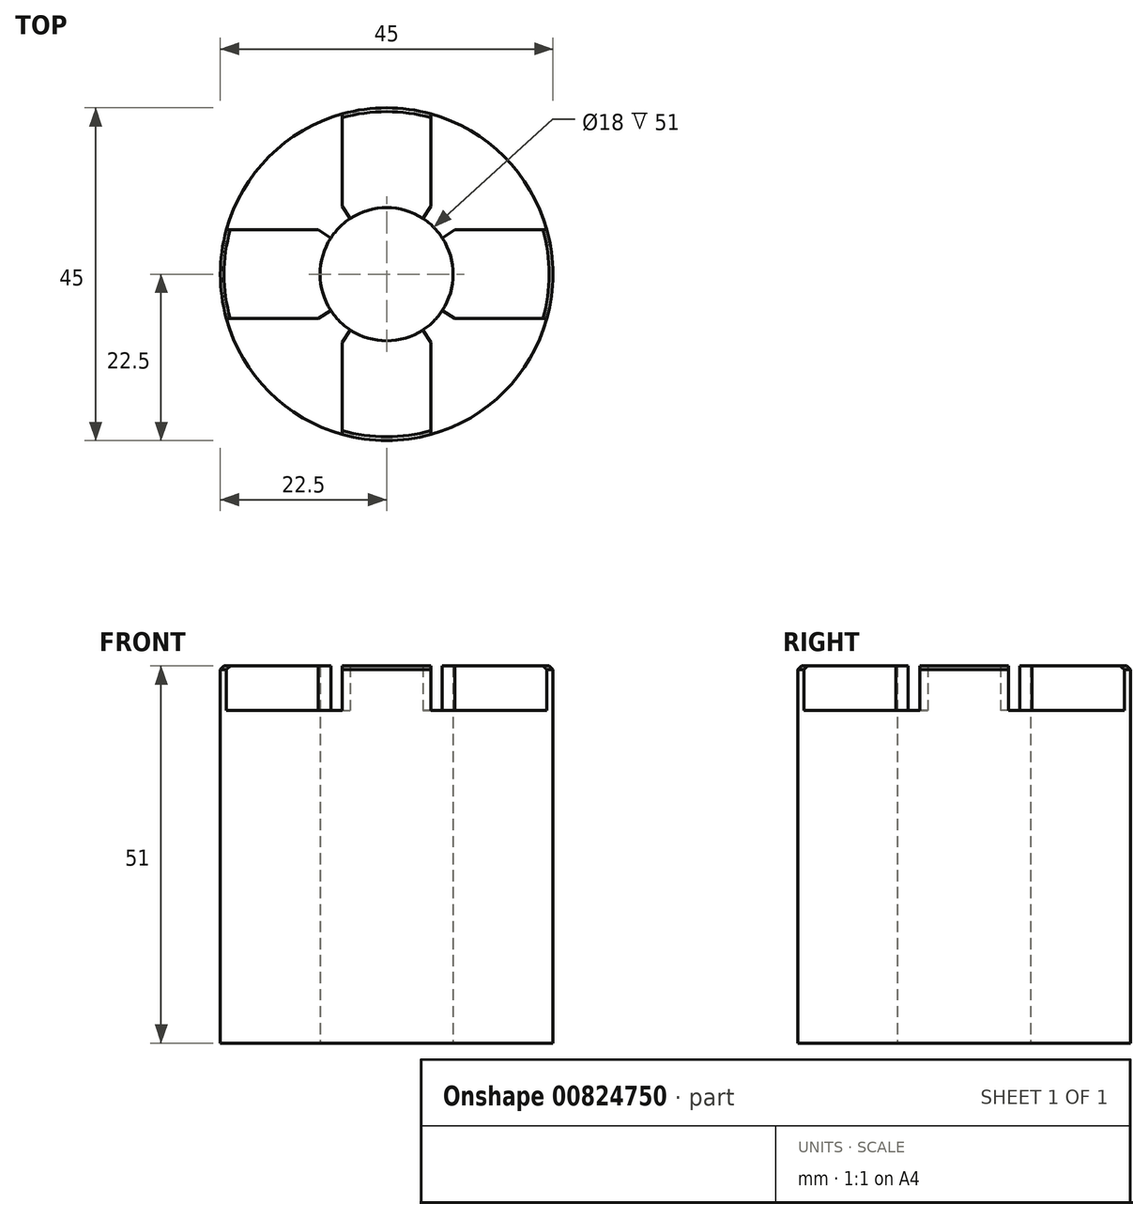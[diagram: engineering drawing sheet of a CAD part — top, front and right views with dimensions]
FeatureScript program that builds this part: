
annotation { "Feature Type Name" : "Feature", "Feature Type Description" : "" }
export const myFeature = defineFeature(function(context is Context, id is Id, definition is map)
    precondition{}
    {
        {
            var Q0;
            Q0=qCreatedBy(makeId("Top.planeOp"),FACE);
            var sketch = newSketch(context, id + "F0", { "sketchPlane" : qUnion([Q0])});
            skCircle(sketch, "E0", {"center": v(0, 0) * mm, "radius": 22.5 * mm});
            skCircle(sketch, "E1", {"center": v(0, 0) * mm, "radius": 9 * mm});
            skSolve(sketch);
        }
        {
            var Q0;
            Q0=makeQuery(id+"F0.imprint","IMPRINT",FACE,{"disambiguationData":[TD([[makeQuery(id+"F0.imprint","IMPRINT",EDGE,{"derivedFrom":sQuery(id+"F0.wireOp",EDGE,"E0")}),1.0]])]});
            extrude(context, id + "F1", {"entities" : qUnion([Q0]), "depth" : 45 * mm, "offsetDistance" : 25 * mm});
        }
        {
            var Q0;
            Q0=makeQuery(id+"F1.opExtrude","CAP_FACE",FACE,{"disambiguationData":[OSD([sQuery(id+"F0.wireOp",EDGE,"E0"),sQuery(id+"F0.wireOp",EDGE,"E1")])],"isStart":false});
            var sketch = newSketch(context, id + "F2", { "sketchPlane" : qUnion([Q0])});
            skLineSegment(sketch, "E2.0", {"start": v(-27.5, -6) * mm, "end": v(-9.22, -6) * mm});
            skLineSegment(sketch, "E3.0", {"start": v(-27.5, 6) * mm, "end": v(-9.22, 6) * mm});
            skLineSegment(sketch, "E4.0", {"start": v(-6, 27.5) * mm, "end": v(-6, 9.22) * mm});
            skLineSegment(sketch, "E5.0", {"start": v(6, 27.5) * mm, "end": v(6, 9.22) * mm});
            skLineSegment(sketch, "E6.bottom", {"start": v(-6, 27.5) * mm, "end": v(6, 27.5) * mm});
            skLineSegment(sketch, "E6.top", {"start": v(-27.5, -27.5) * mm, "end": v(6, -27.5) * mm});
            skLineSegment(sketch, "E6.left", {"start": v(-27.5, 6) * mm, "end": v(-27.5, -6) * mm});
            skLineSegment(sketch, "E6.right", {"start": v(27.5, 6) * mm, "end": v(27.5, -6) * mm});
            skPoint(sketch, "E6.middle", {"position": v(0, 0) * mm});
            skPoint(sketch, "E7.orphan", {"position": v(0, 35.88) * mm});
            skPoint(sketch, "E8.orphan", {"position": v(27.5, 27.5) * mm});
            skPoint(sketch, "E9.orphan", {"position": v(27.5, -27.5) * mm});
            skPoint(sketch, "E10.orphan", {"position": v(-27.5, 27.5) * mm});
            skPoint(sketch, "E11.start.orphan", {"position": v(-29.08, 0) * mm});
            skLineSegment(sketch, "E12.trimOffspring", {"start": v(9.22, 6) * mm, "end": v(27.5, 6) * mm});
            skLineSegment(sketch, "E13.trimOffspring", {"start": v(9.22, -6) * mm, "end": v(27.5, -6) * mm});
            skLineSegment(sketch, "E14.trimOffspring", {"start": v(-6, -9.22) * mm, "end": v(-6, -27.5) * mm});
            skLineSegment(sketch, "E15.trimOffspring", {"start": v(6, -9.22) * mm, "end": v(6, -27.5) * mm});
            skArc(sketch, "E16", {"start": v(4.1, 6.29) * mm, "mid": v(0, 7.5) * mm, "end": v(-4.1, 6.29) * mm});
            skLineSegment(sketch, "E17", {"start": v(-6, 9.22) * mm, "end": v(-4.1, 6.29) * mm});
            skLineSegment(sketch, "E18", {"start": v(6, 9.22) * mm, "end": v(4.1, 6.29) * mm});
            skLineSegment(sketch, "E19", {"start": v(9.22, 6) * mm, "end": v(6.29, 4.1) * mm});
            skLineSegment(sketch, "E20", {"start": v(9.22, -6) * mm, "end": v(6.29, -4.1) * mm});
            skLineSegment(sketch, "E21", {"start": v(6, -9.22) * mm, "end": v(4.1, -6.29) * mm});
            skLineSegment(sketch, "E22", {"start": v(-6, -9.22) * mm, "end": v(-4.1, -6.29) * mm});
            skLineSegment(sketch, "E23", {"start": v(-9.22, -6) * mm, "end": v(-6.29, -4.1) * mm});
            skLineSegment(sketch, "E24", {"start": v(-9.22, 6) * mm, "end": v(-6.29, 4.1) * mm});
            skArc(sketch, "E25.trimOffspring", {"start": v(6.29, -4.1) * mm, "mid": v(7.5, 0) * mm, "end": v(6.29, 4.1) * mm});
            skArc(sketch, "E26.trimOffspring", {"start": v(-4.1, -6.29) * mm, "mid": v(0, -7.5) * mm, "end": v(4.1, -6.29) * mm});
            skArc(sketch, "E27.trimOffspring", {"start": v(-6.29, 4.1) * mm, "mid": v(-7.5, 0) * mm, "end": v(-6.29, -4.1) * mm});
            skSolve(sketch);
        }
        {
            var Q0;
            {var subQ5=sQuery(id+"F2.wireOp",EDGE,"E23");var subQ6=sQuery(id+"F2.wireOp",EDGE,"E2.0");var subQ7=makeQuery(id+"F2.imprint","INTERSECT",VERTEX,{"derivedFrom":[subQ6,subQ5]});Q0=makeQuery(id+"F2.imprint","IMPRINT",FACE,{"disambiguationData":[TD([[makeQuery(id+"F2.imprint","IMPRINT",EDGE,{"disambiguationData":[TD([[subQ7,1.0]])],"derivedFrom":subQ6}),1.0]])]});}
            var Q1;
            {var subQ5=sQuery(id+"F2.wireOp",EDGE,"E4.0");var subQ9=sQuery(id+"F2.wireOp",EDGE,"E17");var subQ10=makeQuery(id+"F2.imprint","INTERSECT",VERTEX,{"derivedFrom":[subQ5,subQ9]});Q1=makeQuery(id+"F2.imprint","IMPRINT",FACE,{"disambiguationData":[TD([[makeQuery(id+"F2.imprint","IMPRINT",EDGE,{"disambiguationData":[TD([[subQ10,1.0]])],"derivedFrom":subQ5}),1.0]])]});}
            var Q2;
            {var subQ0=sQuery(id+"F2.wireOp",EDGE,"E19");var subQ1=sQuery(id+"F2.wireOp",EDGE,"E12.trimOffspring");var subQ2=makeQuery(id+"F2.imprint","INTERSECT",VERTEX,{"derivedFrom":[subQ1,subQ0]});Q2=makeQuery(id+"F2.imprint","IMPRINT",FACE,{"disambiguationData":[TD([[makeQuery(id+"F2.imprint","IMPRINT",EDGE,{"disambiguationData":[TD([[subQ2,-1.0]])],"derivedFrom":subQ1}),-1.0]])]});}
            var Q3;
            {var subQ7=sQuery(id+"F2.wireOp",EDGE,"E22");var subQ8=sQuery(id+"F2.wireOp",EDGE,"E14.trimOffspring");var subQ9=makeQuery(id+"F2.imprint","INTERSECT",VERTEX,{"derivedFrom":[subQ8,subQ7]});Q3=makeQuery(id+"F2.imprint","IMPRINT",FACE,{"disambiguationData":[TD([[makeQuery(id+"F2.imprint","IMPRINT",EDGE,{"disambiguationData":[TD([[subQ9,-1.0]])],"derivedFrom":subQ8}),1.0]])]});}
            extrude(context, id + "F3", {"entities" : qUnion([Q0, Q1, Q2, Q3]), "operationType" : NewBodyOperationType.ADD, "depth" : 6 * mm, "offsetDistance" : 25 * mm});
        }
        {
            var Q0;
            {var subQ0=sQuery(id+"F0.wireOp",EDGE,"E0");var subQ1=makeQuery(id+"F1.opExtrude","CAP_EDGE",EDGE,{"disambiguationData":[OSD([subQ0])],"isStart":false});Q0=makeQuery(id+"F3.opExtrude","CAP_EDGE",EDGE,{"disambiguationData":[OSD([subQ0]),TDD([makeQuery(id+"F2.imprint","IMPRINT",EDGE,{"disambiguationData":[TD([[makeQuery(id+"F2.imprint","INTERSECT",VERTEX,{"derivedFrom":[subQ1,sQuery(id+"F2.wireOp",EDGE,"E2.0")]}),1.0]])],"derivedFrom":subQ1})])],"isStart":false});}
            var Q1;
            {var subQ0=sQuery(id+"F0.wireOp",EDGE,"E0");var subQ1=makeQuery(id+"F1.opExtrude","CAP_EDGE",EDGE,{"disambiguationData":[OSD([subQ0])],"isStart":false});Q1=makeQuery(id+"F3.opExtrude","CAP_EDGE",EDGE,{"disambiguationData":[OSD([subQ0]),TDD([makeQuery(id+"F2.imprint","IMPRINT",EDGE,{"disambiguationData":[TD([[makeQuery(id+"F2.imprint","INTERSECT",VERTEX,{"derivedFrom":[subQ1,sQuery(id+"F2.wireOp",EDGE,"E4.0")]}),1.0]])],"derivedFrom":subQ1})])],"isStart":false});}
            var Q2;
            {var subQ0=sQuery(id+"F0.wireOp",EDGE,"E0");var subQ1=makeQuery(id+"F1.opExtrude","CAP_EDGE",EDGE,{"disambiguationData":[OSD([subQ0])],"isStart":false});Q2=makeQuery(id+"F3.opExtrude","CAP_EDGE",EDGE,{"disambiguationData":[OSD([subQ0]),TDD([makeQuery(id+"F2.imprint","IMPRINT",EDGE,{"disambiguationData":[TD([[makeQuery(id+"F2.imprint","INTERSECT",VERTEX,{"derivedFrom":[subQ1,sQuery(id+"F2.wireOp",EDGE,"E12.trimOffspring")]}),1.0]])],"derivedFrom":subQ1})])],"isStart":false});}
            var Q3;
            {var subQ0=sQuery(id+"F0.wireOp",EDGE,"E0");var subQ1=makeQuery(id+"F1.opExtrude","CAP_EDGE",EDGE,{"disambiguationData":[OSD([subQ0])],"isStart":false});Q3=makeQuery(id+"F3.opExtrude","CAP_EDGE",EDGE,{"disambiguationData":[OSD([subQ0]),TDD([makeQuery(id+"F2.imprint","IMPRINT",EDGE,{"disambiguationData":[TD([[makeQuery(id+"F2.imprint","INTERSECT",VERTEX,{"derivedFrom":[subQ1,sQuery(id+"F2.wireOp",EDGE,"E14.trimOffspring")]}),-1.0]])],"derivedFrom":subQ1})])],"isStart":false});}
            chamfer(context, id + "F4", {"entities" : qUnion([Q0, Q1, Q2, Q3]), "width" : 0.5 * mm, "tangentPropagation" : true});
        }
    });
